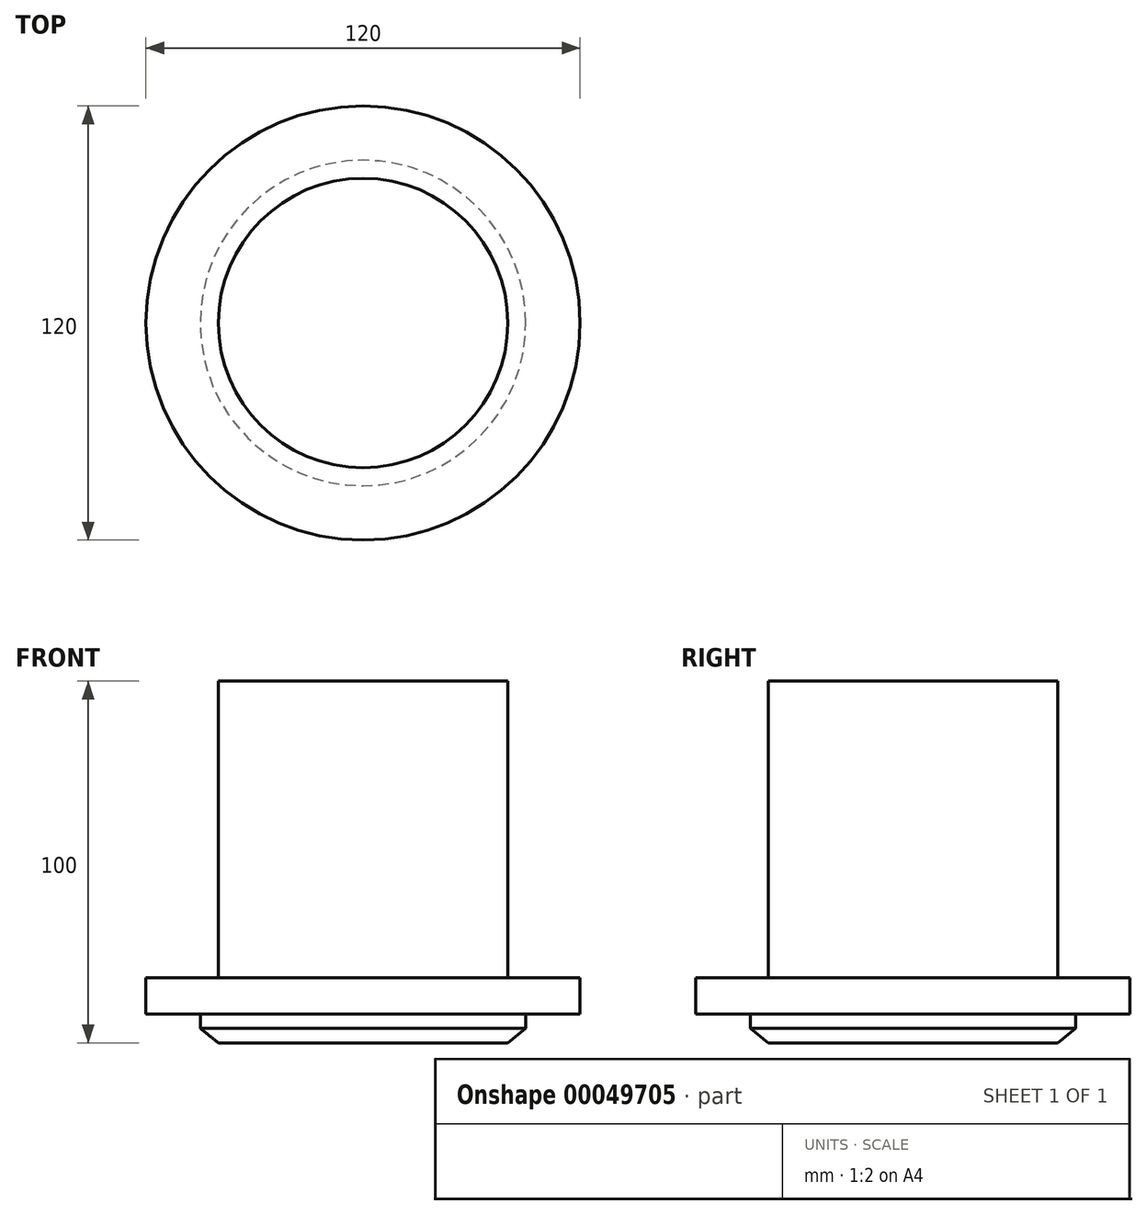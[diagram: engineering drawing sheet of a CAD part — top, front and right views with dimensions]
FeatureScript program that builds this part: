
annotation { "Feature Type Name" : "Feature", "Feature Type Description" : "" }
export const myFeature = defineFeature(function(context is Context, id is Id, definition is map)
    precondition{}
    {
        {
            var Q0;
            Q0=qCreatedBy(makeId("Front.planeOp"),FACE);
            var sketch = newSketch(context, id + "F0", { "sketchPlane" : qUnion([Q0])});
            skLineSegment(sketch, "E0", {"start": v(0, 0) * mm, "end": v(0, 100) * mm});
            skLineSegment(sketch, "E1", {"start": v(0, 100) * mm, "end": v(40, 100) * mm});
            skLineSegment(sketch, "E2", {"start": v(40, 100) * mm, "end": v(40, 18) * mm});
            skLineSegment(sketch, "E3", {"start": v(40, 18) * mm, "end": v(60, 18) * mm});
            skLineSegment(sketch, "E4", {"start": v(60, 18) * mm, "end": v(60, 8) * mm});
            skLineSegment(sketch, "E5", {"start": v(60, 8) * mm, "end": v(45, 8) * mm});
            skLineSegment(sketch, "E6", {"start": v(45, 8) * mm, "end": v(45, 4) * mm});
            skLineSegment(sketch, "E7", {"start": v(45, 4) * mm, "end": v(40, 0) * mm});
            skLineSegment(sketch, "E8", {"start": v(40, 0) * mm, "end": v(0, 0) * mm});
            skSolve(sketch);
        }
        {
            var Q0;
            Q0 = qSketchRegion(id + "F0", true);
            var Q1;
            Q1=sQuery(id+"F0.wireOp",EDGE,"E0");
            revolve(context, id + "F1", {"entities" : qUnion([Q0]), "axis" : qUnion([Q1]), "revolveType" : RevolveType.FULL});
        }
    });
